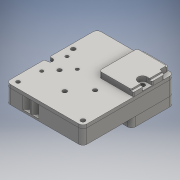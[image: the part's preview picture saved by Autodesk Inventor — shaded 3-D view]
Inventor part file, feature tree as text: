
AUTODESK INVENTOR PART (.ipt)
format: ipt  version: 2016 (Build 200138000, 138)  size: 1,059,840 bytes
history: native  units: mm
features: extrude x20, other x15, sketch x5, fillet x4, hole x2, mirror x1, projected_geometry x1
ambient origin geometry x8: Origin, YZ Plane, XZ Plane, XY Plane, X Axis, Y Axis, Z Axis, Center Point
bodies: Body1 (feature_tree), Body2 (feature_tree), Body3 (feature_tree), Body4 (feature_tree), Body5 (feature_tree)
feature tree (48):
  other  "top_channel"
  other  "Plan"
  other  "top channel sketch"
  extrude  "floor of top channel"  Depth=45.0mm
  extrude  "topchannel"  Depth=17.0mm
  other  "bottom channel sketch"
  extrude  "bottom channel solid"  Depth=1.397mm
  extrude  "bottom channel void"  Depth=20.0mm
  extrude  "bottom channel vanes"  Depth=25.0mm
  extrude  "pcb_solid"  Depth=20.0mm
  other  "light trap sketch"
  extrude  "light trap"  Depth=1.6mm
  other  "laser_holder_sketch"
  extrude  "laser_holder_solid"  Depth=1.6mm
  extrude  "aperture1"  Depth=1.2mm
  extrude  "aperture 2"  Depth=1.5mm
  extrude  "aperture 3"  Depth=3.0mm
  extrude  "laser_holder_void"  Depth=1.5mm
  other  "mirro plane for laser holder"
  hole  "mounting laser holes"  [1 undecoded]
  fillet  "fillet for laser holder"  Radius=5.0mm
  mirror  "flip the laser holder"
  extrude  "light aperture from opposite side of laser"  Depth=3.0mm
  fillet  "most other fillets"  Radius=3.0mm
  hole  "Hole2"  [1 undecoded]
  extrude  "cap_solid"  TaperAngle=60.0deg  [1 undecoded]
  extrude  "full cuts"  Depth=1.5mm
  other  "analog_cap_screw_sketch"
  extrude  "screw seat"  Depth=1.5mm
  extrude  "screw hole"  Depth=1.5mm
  extrude  "Extrusion24"  Depth=1.5mm
  extrude  "core"  Depth=1.5mm
  extrude  "room for adc"  Depth=2.0mm
  fillet  "most fillets"  Radius=1.5mm
  fillet  "smaller_fillets"  Radius=1.5875mm
  other  "bottom_channel"
  other  "floor sketch"
  other  "pcb sketch"
  other  "pcb"
  other  "vanes sketch"
  other  "laser_holder"
  sketch  "Sketch13"  dims[d0=38.0mm d1=45.0mm]
  sketch  "Sketch15"  dims[d2=17.0mm d3=0.65mm]
  other  "analog_cap"
  sketch  "Sketch16"  dims[d4=11.3mm d5=1.397mm]
  projected_geometry  "Projected Loop3"
  sketch  "Sketch19"  dims[d6=6.0mm d7=20.0mm]
  sketch  "Sketch21"  dims[d8=37.0mm d9=25.0mm d10=20.0mm d11=1.6mm d12=1.6mm d13=3.95mm d14=1.5mm d15=3.0mm d17=6.0mm d18=1.5mm d19=5.0mm d20=5.0mm d21=3.0mm d22=3.0mm d23=60.0deg d24=60.0deg d26=1.5mm d27=1.5mm d28=1.5mm d30=1.5mm d31=1.5mm d32=2.0mm d33=1.5mm d34=1.5875mm d37=2.0mm d39=8.0mm d41=7.1mm d42=0.0mm d43=3.490659mm d44=1.5mm d46=1.5mm d48=1.5mm d51=1.5mm d52=1.5mm d62=4.5mm d63=0.0mm d64=3.5mm d65=0.0mm d77=1.0mm d78=0.0mm d79=1.65mm d80=0.0mm d86=1.25mm d88=2.0mm d89=2.5mm d90=1.5mm d96=1.5mm d97=1.5mm d98=1.5mm d99=1.5mm d104=2.0mm d106=2.54mm d107=1.5mm d109=1.397mm d111=0.5mm d113=3.0mm d115=13.5mm d116=2.1mm d117=2.1mm d121=1.0mm d124=1.8mm d125=2.1mm d126=2.1mm d127=2.1mm d128=2.5mm d130=2.120272mm d132=13.0mm d134=2.1mm d136=1.5mm d138=5.585054mm d140=10.0mm d141=0.0mm d143=1.5875mm d144=1.5875mm d145=2.0mm d146=6.0mm d147=2.5mm d154=3.0mm d157=3.0mm d160=0.5mm d162=10.0mm d163=0.0mm d165=5.0mm d167=8.185575mm d169=1.397mm d170=4.0mm d171=6.0mm d172=6.0mm d173=1.5mm d174=0.8mm d175=1.5mm d176=1.5mm d177=5.5mm d178=1.5mm d179=3.490659mm d180=3.0mm d181=0.5mm d182=2.0875mm d183=2.7mm d184=3.5mm d185=6.0mm d186=0.0mm d187=1.5875mm d188=4.75mm d189=0.0mm d190=4.35mm d191=0.0mm d192=4.04mm d193=0.0mm d194=4.04mm d195=0.0mm d197=1.5875mm d198=6.0mm d199=4.8625mm d200=3.675mm d201=90.0deg d202=8.0mm d203=20.594885mm d204=0.79375mm d206=1.5875mm d208=1.5mm d209=5.5mm d210=1.96mm d211=0.0mm d212=2.1mm d213=10.5mm d214=18.5mm d215=1.5mm d218=2.0mm d219=1.5875mm d220=3.0875mm d221=1.0mm d222=0.79375mm d223=0.5mm d226=1.0mm d228=0.1mm d232=1.5mm d233=10.0mm d234=5.0mm d235=0.5mm d236=1.5mm d237=1.5875mm d238=4.363323mm d239=1.5mm d243=2.5mm d244=2.0mm d254=8.0mm d255=8.760777mm d256=14.3mm d257=0.6mm d258=14.3mm d259=1.5875mm d263=2.0mm d264=6.0mm d265=4.0mm d266=2.0mm d267=90.0deg d268=8.0mm d269=20.594885mm d275=2.75mm d276=2.75mm d277=2.75mm d278=2.25mm d279=12.5mm d280=1.25mm d291=1.5mm d292=3.175mm d293=1.5875mm d294=1.5875mm d295=0.8mm d296=1.6mm d297=1.1mm d298=0.3mm d299=1.5875mm d300=5.0mm d301=3.0mm d302=17.0mm d303=20.0mm d304=2.8mm d305=0.0mm d306=2.5mm d307=4.5mm d308=2.0mm d309=1.0mm d310=3.0mm d311=0.0mm d312=2.2mm d316=2.4mm d317=0.0mm d318=2.8mm d319=0.0mm d323=1.5mm d324=0.0mm d325=0.5mm d326=1.0mm d327=0.25mm d328=1.5mm d329=1.5mm d330=0.0mm d331=5.0mm d334=4.4mm d336=0.8mm d347=0.8mm d348=0.0mm d349=1.2mm]
note: 3 required parameter values undecoded (feature->parameter linkage not recoverable at this tier; creation-order binding heuristic only, values carry confidence <= 0.55)
